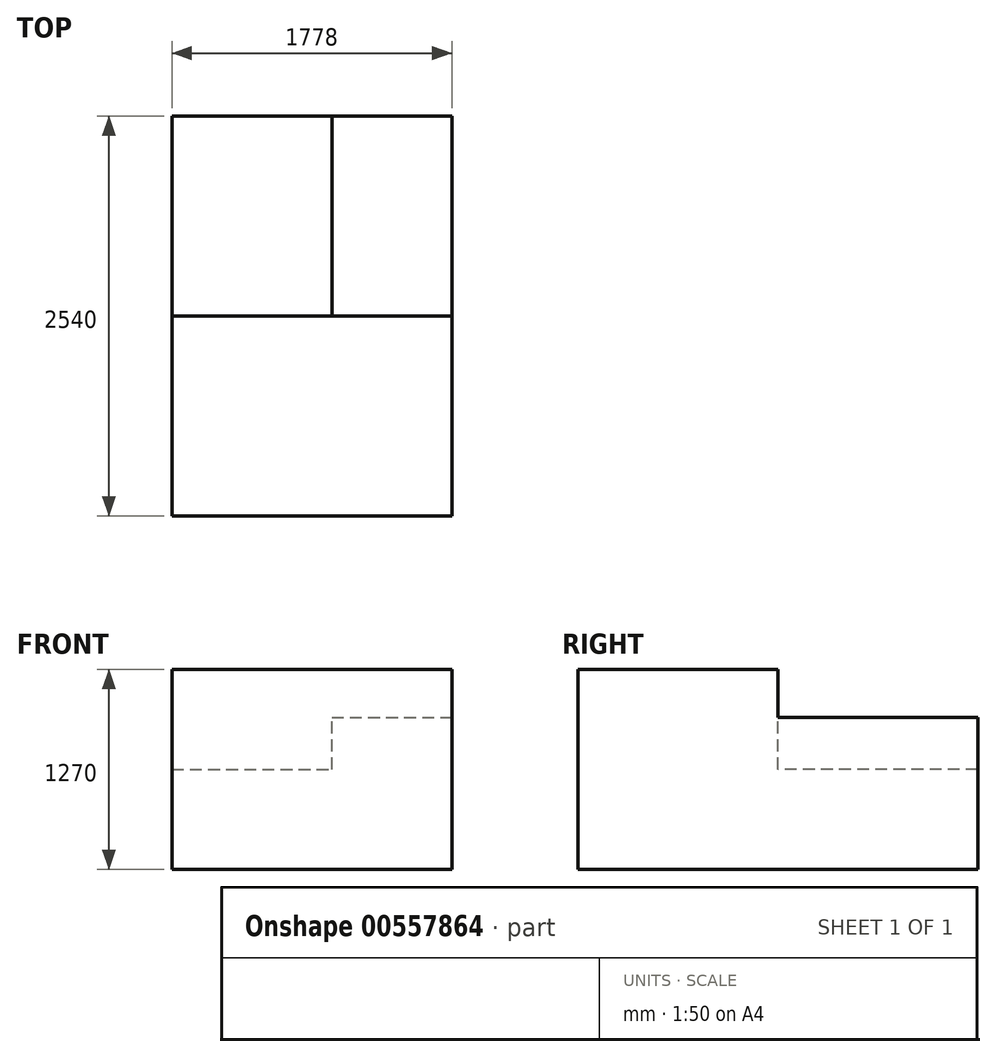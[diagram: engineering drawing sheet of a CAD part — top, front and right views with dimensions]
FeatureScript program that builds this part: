
annotation { "Feature Type Name" : "Feature", "Feature Type Description" : "" }
export const myFeature = defineFeature(function(context is Context, id is Id, definition is map)
    precondition{}
    {
        {
            var Q0;
            Q0=qCreatedBy(makeId("Top.planeOp"),FACE);
            var sketch = newSketch(context, id + "F0", { "sketchPlane" : qUnion([Q0])});
            skLineSegment(sketch, "E0", {"start": v(-142.05, 73.94) * mm, "end": v(1635.95, 73.94) * mm});
            skLineSegment(sketch, "E1", {"start": v(1635.95, 73.94) * mm, "end": v(1635.95, -2466.06) * mm});
            skLineSegment(sketch, "E2", {"start": v(-142.05, 73.94) * mm, "end": v(-142.05, -2466.06) * mm});
            skLineSegment(sketch, "E3", {"start": v(-142.05, -2466.06) * mm, "end": v(1635.95, -2466.06) * mm});
            skLineSegment(sketch, "E4", {"start": v(1635.95, -2466.06) * mm, "end": v(1635.95, -1196.06) * mm});
            skLineSegment(sketch, "E5", {"start": v(1635.95, -1196.06) * mm, "end": v(-142.05, -1196.06) * mm});
            skLineSegment(sketch, "E6", {"start": v(-142.05, -1196.06) * mm, "end": v(-142.05, 73.94) * mm});
            skLineSegment(sketch, "E7", {"start": v(-142.05, 73.94) * mm, "end": v(873.95, 73.94) * mm});
            skLineSegment(sketch, "E8", {"start": v(873.95, 73.94) * mm, "end": v(873.95, -1196.06) * mm});
            skSolve(sketch);
        }
        {
            var Q0;
            Q0 = qSketchRegion(id + "F0", true);
            extrude(context, id + "F1", {"entities" : qUnion([Q0]), "oppositeDirection" : true, "depth" : 1270 * mm, "offsetDistance" : 25.4 * mm});
        }
        {
            var Q0;
            Q0=makeQuery(id+"F0.imprint","IMPRINT",FACE,{"disambiguationData":[TD([[makeQuery(id+"F0.imprint","IMPRINT",EDGE,{"derivedFrom":sQuery(id+"F0.wireOp",EDGE,"E0")}),-1.0]])]});
            extrude(context, id + "F2", {"entities" : qUnion([Q0]), "operationType" : NewBodyOperationType.REMOVE, "oppositeDirection" : true, "depth" : 304.8 * mm, "offsetDistance" : 25.4 * mm});
        }
        {
            var Q0;
            {var subQ3=sQuery(id+"F0.wireOp",EDGE,"E2");Q0=makeQuery(id+"F0.imprint","IMPRINT",FACE,{"disambiguationData":[TD([[makeQuery(id+"F0.imprint","IMPRINT",EDGE,{"derivedFrom":subQ3}),1.0]])]});}
            extrude(context, id + "F3", {"entities" : qUnion([Q0]), "operationType" : NewBodyOperationType.REMOVE, "oppositeDirection" : true, "depth" : 635 * mm, "offsetDistance" : 25.4 * mm});
        }
    });
